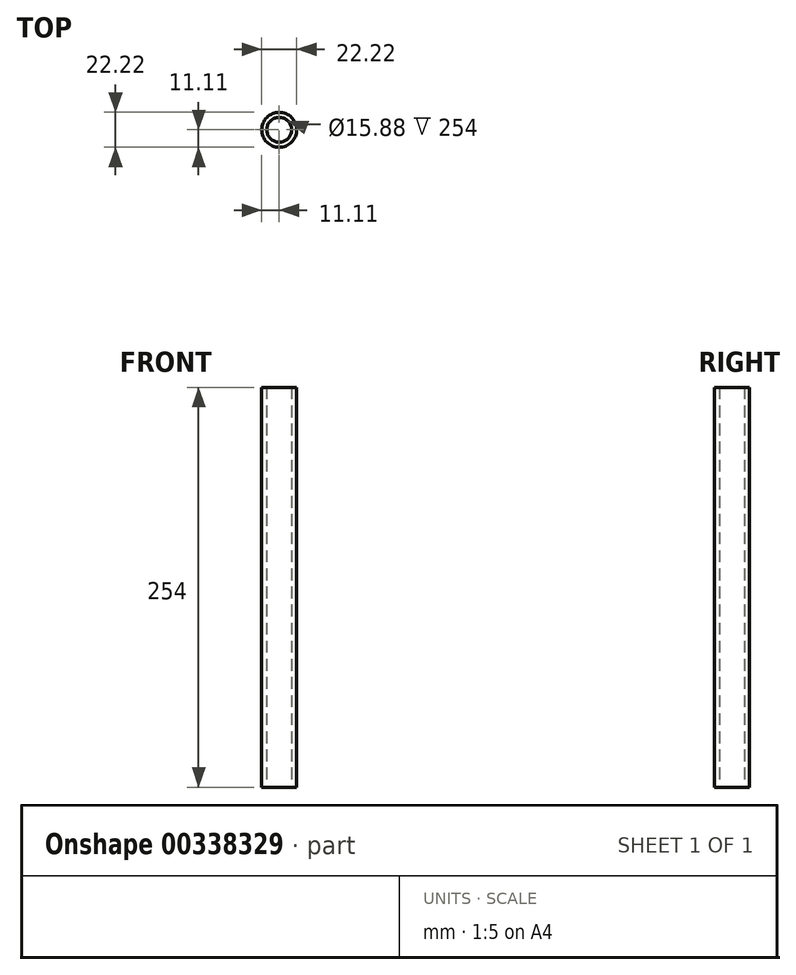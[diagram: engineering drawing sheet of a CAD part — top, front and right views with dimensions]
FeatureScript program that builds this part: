
annotation { "Feature Type Name" : "Feature", "Feature Type Description" : "" }
export const myFeature = defineFeature(function(context is Context, id is Id, definition is map)
    precondition{}
    {
        {
            var Q0;
            Q0=qCreatedBy(makeId("Top.planeOp"),FACE);
            var sketch = newSketch(context, id + "F0", { "sketchPlane" : qUnion([Q0])});
            skCircle(sketch, "E0", {"center": v(0, 0) * mm, "radius": 7.94 * mm});
            skCircle(sketch, "E1", {"center": v(0, 0) * mm, "radius": 11.11 * mm});
            skSolve(sketch);
        }
        {
            var Q0;
            Q0 = qSketchRegion(id + "F0", true);
            extrude(context, id + "F1", {"entities" : qUnion([Q0]), "depth" : 254 * mm});
        }
    });
